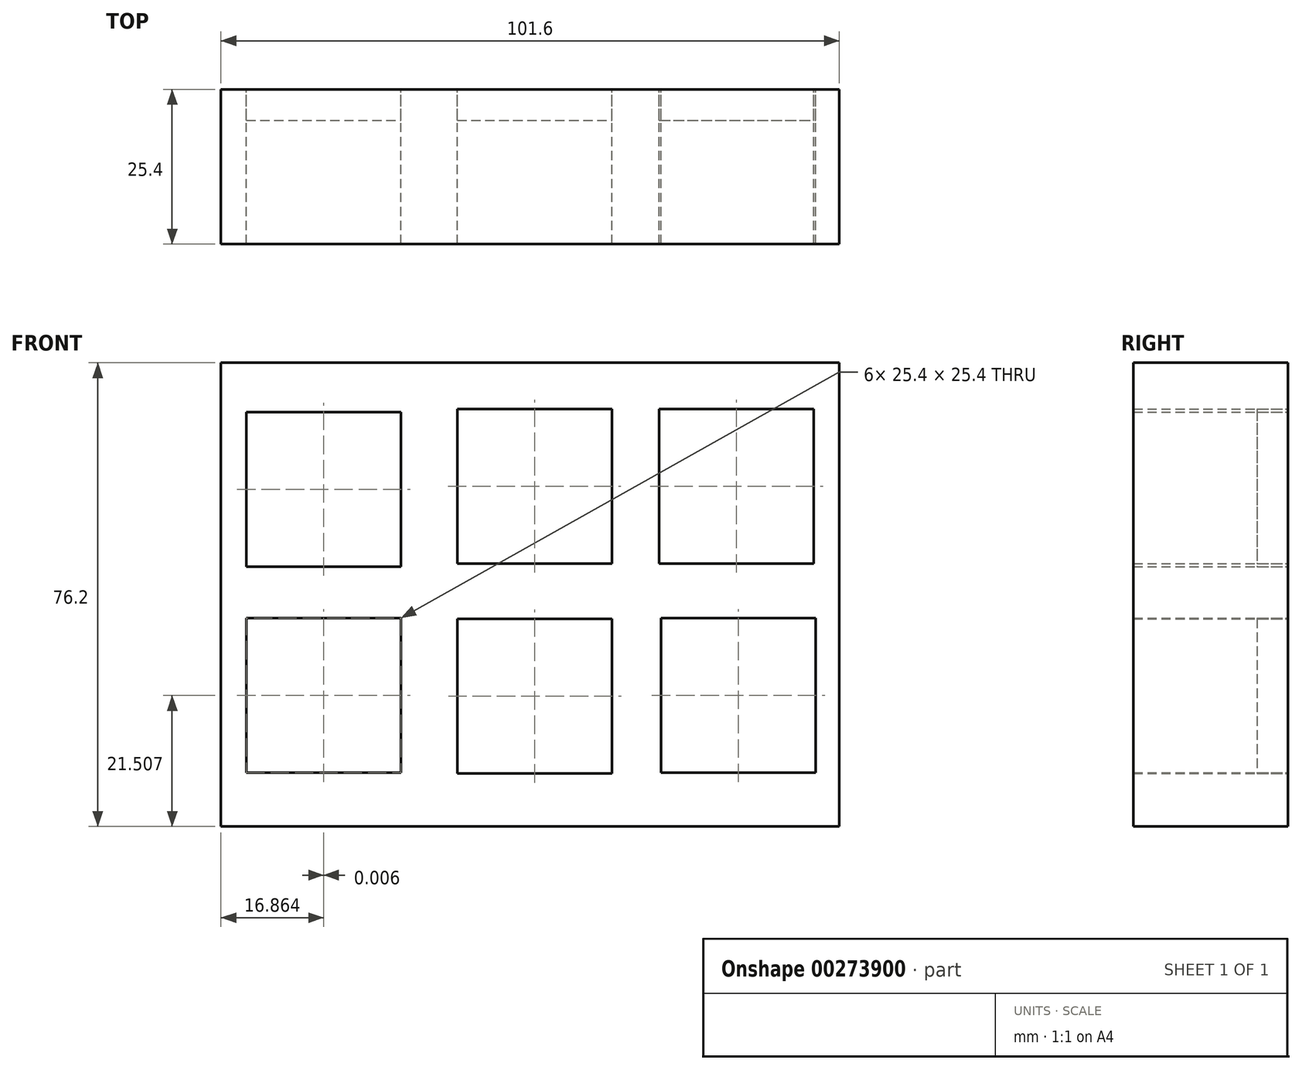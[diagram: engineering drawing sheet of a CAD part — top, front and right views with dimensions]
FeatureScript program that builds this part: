
annotation { "Feature Type Name" : "Feature", "Feature Type Description" : "" }
export const myFeature = defineFeature(function(context is Context, id is Id, definition is map)
    precondition{}
    {
        {
            var Q0;
            Q0=qCreatedBy(makeId("Front.planeOp"),FACE);
            var sketch = newSketch(context, id + "F0", { "sketchPlane" : qUnion([Q0])});
            skLineSegment(sketch, "E0.bottom", {"start": v(-50.8, 38.1) * mm, "end": v(50.8, 38.1) * mm});
            skLineSegment(sketch, "E0.top", {"start": v(-50.8, -38.1) * mm, "end": v(50.8, -38.1) * mm});
            skLineSegment(sketch, "E0.left", {"start": v(-50.8, 38.1) * mm, "end": v(-50.8, -38.1) * mm});
            skLineSegment(sketch, "E0.right", {"start": v(50.8, 38.1) * mm, "end": v(50.8, -38.1) * mm});
            skPoint(sketch, "E0.middle", {"position": v(0, 0) * mm});
            skLineSegment(sketch, "E1.bottom", {"start": v(-46.63, 30) * mm, "end": v(-21.23, 30) * mm});
            skLineSegment(sketch, "E1.top", {"start": v(-46.63, 4.6) * mm, "end": v(-21.23, 4.6) * mm});
            skLineSegment(sketch, "E1.left", {"start": v(-46.63, 30) * mm, "end": v(-46.63, 4.6) * mm});
            skLineSegment(sketch, "E1.right", {"start": v(-21.23, 30) * mm, "end": v(-21.23, 4.6) * mm});
            skLineSegment(sketch, "E2.bottom", {"start": v(-12, 30.5) * mm, "end": v(13.4, 30.5) * mm});
            skLineSegment(sketch, "E2.top", {"start": v(-12, 5.1) * mm, "end": v(13.4, 5.1) * mm});
            skLineSegment(sketch, "E2.left", {"start": v(-12, 30.5) * mm, "end": v(-12, 5.1) * mm});
            skLineSegment(sketch, "E2.right", {"start": v(13.4, 30.5) * mm, "end": v(13.4, 5.1) * mm});
            skLineSegment(sketch, "E3.bottom", {"start": v(21.22, 30.5) * mm, "end": v(46.62, 30.5) * mm});
            skLineSegment(sketch, "E3.top", {"start": v(21.22, 5.1) * mm, "end": v(46.62, 5.1) * mm});
            skLineSegment(sketch, "E3.left", {"start": v(21.22, 30.5) * mm, "end": v(21.22, 5.1) * mm});
            skLineSegment(sketch, "E3.right", {"start": v(46.62, 30.5) * mm, "end": v(46.62, 5.1) * mm});
            skLineSegment(sketch, "E4.bottom", {"start": v(21.5, -3.9) * mm, "end": v(46.9, -3.9) * mm});
            skLineSegment(sketch, "E4.top", {"start": v(21.5, -29.3) * mm, "end": v(46.9, -29.3) * mm});
            skLineSegment(sketch, "E4.left", {"start": v(21.5, -3.9) * mm, "end": v(21.5, -29.3) * mm});
            skLineSegment(sketch, "E4.right", {"start": v(46.9, -3.9) * mm, "end": v(46.9, -29.3) * mm});
            skLineSegment(sketch, "E5.bottom", {"start": v(-11.95, -3.98) * mm, "end": v(13.45, -3.98) * mm});
            skLineSegment(sketch, "E5.top", {"start": v(-11.95, -29.38) * mm, "end": v(13.45, -29.38) * mm});
            skLineSegment(sketch, "E5.left", {"start": v(-11.95, -3.98) * mm, "end": v(-11.95, -29.38) * mm});
            skLineSegment(sketch, "E5.right", {"start": v(13.45, -3.98) * mm, "end": v(13.45, -29.38) * mm});
            skLineSegment(sketch, "E6.bottom", {"start": v(-46.64, -3.9) * mm, "end": v(-21.24, -3.9) * mm});
            skLineSegment(sketch, "E6.top", {"start": v(-46.64, -29.3) * mm, "end": v(-21.24, -29.3) * mm});
            skLineSegment(sketch, "E6.left", {"start": v(-46.64, -3.9) * mm, "end": v(-46.64, -29.3) * mm});
            skLineSegment(sketch, "E6.right", {"start": v(-21.24, -3.9) * mm, "end": v(-21.24, -29.3) * mm});
            skSolve(sketch);
        }
        {
            var Q0;
            Q0 = qSketchRegion(id + "F0", true);
            extrude(context, id + "F1", {"entities" : qUnion([Q0]), "depth" : 25.4 * mm});
        }
        {
            var Q0;
            Q0=makeQuery(id+"F0.imprint","IMPRINT",FACE,{"disambiguationData":[TD([[makeQuery(id+"F0.imprint","IMPRINT",EDGE,{"derivedFrom":sQuery(id+"F0.wireOp",EDGE,"E1.bottom")}),-1.0]])]});
            var Q1;
            Q1=makeQuery(id+"F0.imprint","IMPRINT",FACE,{"disambiguationData":[TD([[makeQuery(id+"F0.imprint","IMPRINT",EDGE,{"derivedFrom":sQuery(id+"F0.wireOp",EDGE,"E2.bottom")}),-1.0]])]});
            var Q2;
            Q2=makeQuery(id+"F0.imprint","IMPRINT",FACE,{"disambiguationData":[TD([[makeQuery(id+"F0.imprint","IMPRINT",EDGE,{"derivedFrom":sQuery(id+"F0.wireOp",EDGE,"E3.bottom")}),-1.0]])]});
            var Q3;
            Q3=makeQuery(id+"F0.imprint","IMPRINT",FACE,{"disambiguationData":[TD([[makeQuery(id+"F0.imprint","IMPRINT",EDGE,{"derivedFrom":sQuery(id+"F0.wireOp",EDGE,"E4.bottom")}),-1.0]])]});
            var Q4;
            Q4=makeQuery(id+"F0.imprint","IMPRINT",FACE,{"disambiguationData":[TD([[makeQuery(id+"F0.imprint","IMPRINT",EDGE,{"derivedFrom":sQuery(id+"F0.wireOp",EDGE,"E5.bottom")}),-1.0]])]});
            var Q5;
            Q5=makeQuery(id+"F0.imprint","IMPRINT",FACE,{"disambiguationData":[TD([[makeQuery(id+"F0.imprint","IMPRINT",EDGE,{"derivedFrom":sQuery(id+"F0.wireOp",EDGE,"E6.bottom")}),-1.0]])]});
            extrude(context, id + "F2", {"entities" : qUnion([Q0, Q1, Q2, Q3, Q4, Q5]), "depth" : 5.08 * mm});
        }
    });
